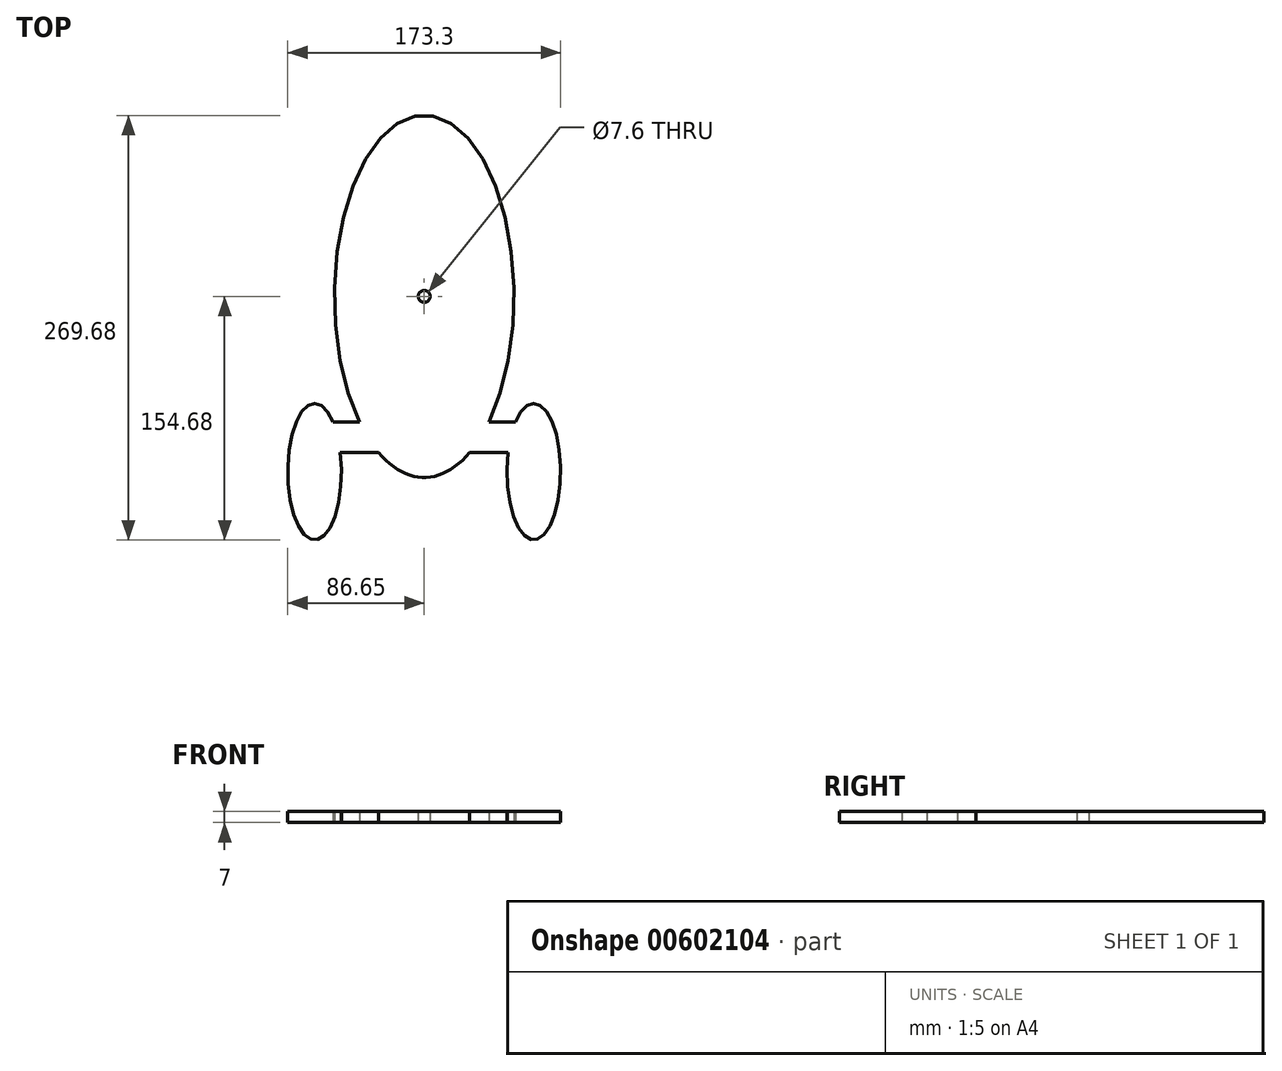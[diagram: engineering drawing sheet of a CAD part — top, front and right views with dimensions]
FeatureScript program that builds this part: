
annotation { "Feature Type Name" : "Feature", "Feature Type Description" : "" }
export const myFeature = defineFeature(function(context is Context, id is Id, definition is map)
    precondition{}
    {
        {
            var Q0;
            Q0=qCreatedBy(makeId("Top.planeOp"),FACE);
            var sketch = newSketch(context, id + "F0", { "sketchPlane" : qUnion([Q0])});
            skLineSegment(sketch, "E0", {"start": v(0, 0) * mm, "end": v(0, -115) * mm});
            skEllipse(sketch, "E1", {"center": v(0, 0) * mm, "majorRadius": 115 * mm, "minorRadius": 57 * mm, "majorAxis": v(0, -1)});
            skEllipse(sketch, "E2", {"center": v(-69.6, -111.35) * mm, "majorRadius": 43.33 * mm, "minorRadius": 17.04 * mm, "majorAxis": v(0, -1)});
            skLineSegment(sketch, "E3.bottom", {"start": v(-66.85, -79.83) * mm, "end": v(-14.85, -79.83) * mm});
            skLineSegment(sketch, "E3.top", {"start": v(-66.85, -99.13) * mm, "end": v(-14.85, -99.13) * mm});
            skLineSegment(sketch, "E3.left", {"start": v(-66.85, -79.83) * mm, "end": v(-66.85, -99.13) * mm});
            skLineSegment(sketch, "E3.right", {"start": v(-14.85, -79.83) * mm, "end": v(-14.85, -99.13) * mm});
            skLineSegment(sketch, "E4.MirrorCS", {"start": v(14.85, -79.83) * mm, "end": v(14.85, -99.13) * mm});
            skLineSegment(sketch, "E5.MirrorCS", {"start": v(66.85, -79.83) * mm, "end": v(14.85, -79.83) * mm});
            skLineSegment(sketch, "E6.MirrorCS", {"start": v(66.85, -79.83) * mm, "end": v(66.85, -99.13) * mm});
            skEllipse(sketch, "E7.MirrorC", {"center": v(69.6, -111.35) * mm, "majorRadius": 43.33 * mm, "minorRadius": 17.04 * mm, "majorAxis": v(0, -1)});
            skLineSegment(sketch, "E8.MirrorCS", {"start": v(66.85, -99.13) * mm, "end": v(14.85, -99.13) * mm});
            skCircle(sketch, "E9", {"center": v(0, 0) * mm, "radius": 3.8 * mm});
            skSolve(sketch);
        }
        {
            var Q0;
            {var subQ5=sQuery(id+"F0.wireOp",EDGE,"E3.left");Q0=makeQuery(id+"F0.imprint","IMPRINT",FACE,{"disambiguationData":[TD([[makeQuery(id+"F0.imprint","IMPRINT",EDGE,{"derivedFrom":subQ5}),-1.0]])]});}
            var Q1;
            {var subQ0=sQuery(id+"F0.wireOp",EDGE,"E6.MirrorCS");Q1=makeQuery(id+"F0.imprint","IMPRINT",FACE,{"disambiguationData":[TD([[makeQuery(id+"F0.imprint","IMPRINT",EDGE,{"derivedFrom":subQ0}),1.0]])]});}
            var Q2;
            {var subQ5=sQuery(id+"F0.wireOp",EDGE,"E4.MirrorCS");Q2=makeQuery(id+"F0.imprint","IMPRINT",FACE,{"disambiguationData":[TD([[makeQuery(id+"F0.imprint","IMPRINT",EDGE,{"derivedFrom":subQ5}),1.0]])]});}
            var Q3;
            {var subQ0=sQuery(id+"F0.wireOp",EDGE,"E8.MirrorCS");var subQ1=sQuery(id+"F0.wireOp",EDGE,"E1");var subQ2=makeQuery(id+"F0.imprint","INTERSECT",VERTEX,{"derivedFrom":[subQ1,subQ0]});Q3=makeQuery(id+"F0.imprint","IMPRINT",FACE,{"disambiguationData":[TD([[makeQuery(id+"F0.imprint","IMPRINT",EDGE,{"disambiguationData":[TD([[subQ2,-1.0]])],"derivedFrom":subQ1}),-1.0]])]});}
            var Q4;
            {var subQ0=sQuery(id+"F0.wireOp",EDGE,"E3.bottom");var subQ1=sQuery(id+"F0.wireOp",EDGE,"E1");var subQ2=makeQuery(id+"F0.imprint","INTERSECT",VERTEX,{"derivedFrom":[subQ1,subQ0]});Q4=makeQuery(id+"F0.imprint","IMPRINT",FACE,{"disambiguationData":[TD([[makeQuery(id+"F0.imprint","IMPRINT",EDGE,{"disambiguationData":[TD([[subQ2,-1.0]])],"derivedFrom":subQ1}),-1.0]])]});}
            var Q5;
            {var subQ5=sQuery(id+"F0.wireOp",EDGE,"E3.right");Q5=makeQuery(id+"F0.imprint","IMPRINT",FACE,{"disambiguationData":[TD([[makeQuery(id+"F0.imprint","IMPRINT",EDGE,{"derivedFrom":subQ5}),-1.0]])]});}
            var Q6;
            {var subQ5=sQuery(id+"F0.wireOp",EDGE,"E3.left");Q6=makeQuery(id+"F0.imprint","IMPRINT",FACE,{"disambiguationData":[TD([[makeQuery(id+"F0.imprint","IMPRINT",EDGE,{"derivedFrom":subQ5}),1.0]])]});}
            var Q7;
            {var subQ0=sQuery(id+"F0.wireOp",EDGE,"E6.MirrorCS");Q7=makeQuery(id+"F0.imprint","IMPRINT",FACE,{"disambiguationData":[TD([[makeQuery(id+"F0.imprint","IMPRINT",EDGE,{"derivedFrom":subQ0}),-1.0]])]});}
            var Q8;
            {var subQ0=sQuery(id+"F0.wireOp",EDGE,"E3.right");Q8=makeQuery(id+"F0.imprint","IMPRINT",FACE,{"disambiguationData":[TD([[makeQuery(id+"F0.imprint","IMPRINT",EDGE,{"derivedFrom":subQ0}),1.0]])]});}
            extrude(context, id + "F1", {"entities" : qUnion([Q0, Q1, Q2, Q3, Q4, Q5, Q6, Q7, Q8]), "depth" : 7 * mm, "offsetDistance" : 25 * mm});
        }
    });
